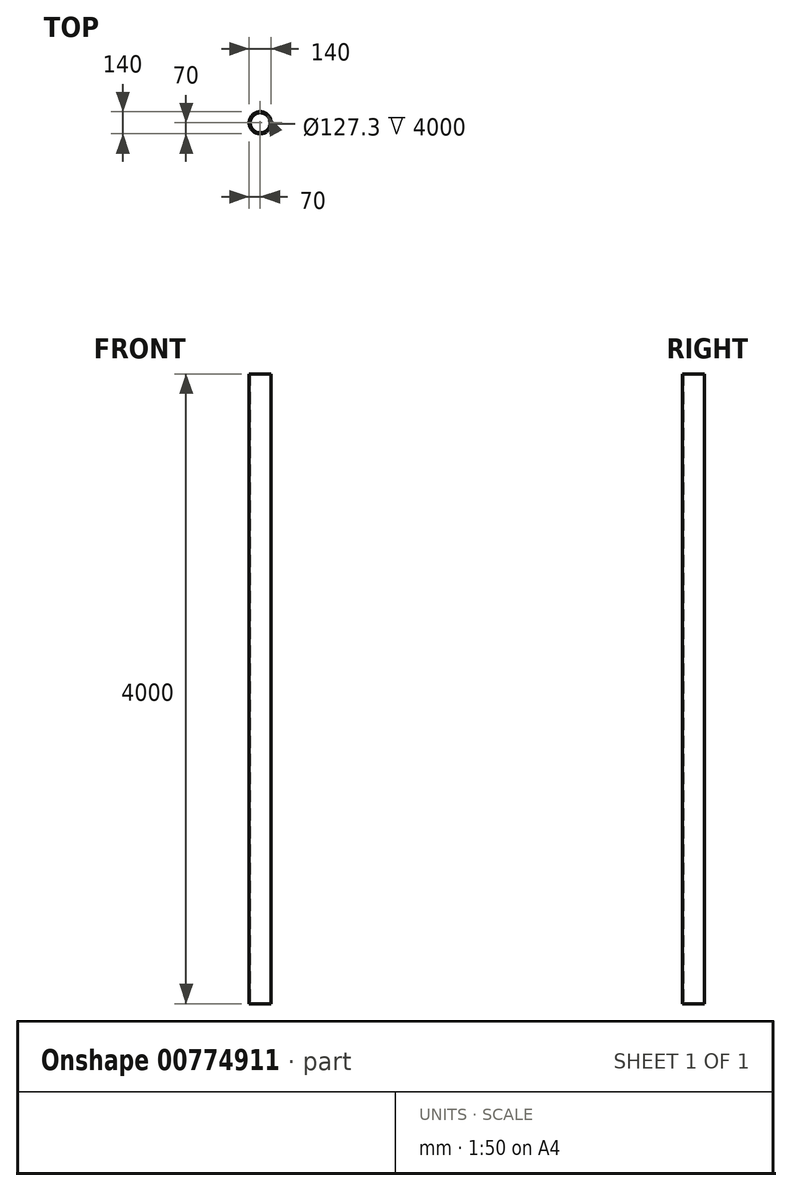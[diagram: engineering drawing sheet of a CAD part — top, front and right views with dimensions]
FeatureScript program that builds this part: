
annotation { "Feature Type Name" : "Feature", "Feature Type Description" : "" }
export const myFeature = defineFeature(function(context is Context, id is Id, definition is map)
    precondition{}
    {
        {
            var Q0;
            Q0=qCreatedBy(makeId("Top.planeOp"),FACE);
            var sketch = newSketch(context, id + "F0", { "sketchPlane" : qUnion([Q0])});
            skCircle(sketch, "E0", {"center": v(0, 0) * mm, "radius": 70 * mm});
            skCircle(sketch, "E1", {"center": v(0, 0) * mm, "radius": 63.65 * mm});
            skSolve(sketch);
        }
        {
            var Q0;
            Q0=makeQuery(id+"F0.imprint","IMPRINT",FACE,{"disambiguationData":[TD([[makeQuery(id+"F0.imprint","IMPRINT",EDGE,{"derivedFrom":sQuery(id+"F0.wireOp",EDGE,"E0")}),1.0]])]});
            extrude(context, id + "F1", {"entities" : qUnion([Q0]), "depth" : 4000 * mm, "offsetDistance" : 25 * mm});
        }
    });
